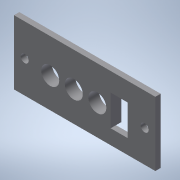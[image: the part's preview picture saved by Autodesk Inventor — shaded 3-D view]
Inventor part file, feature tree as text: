
AUTODESK INVENTOR PART (.ipt)
format: ipt  version: 2020 (Build 240168000, 168)  size: 364,544 bytes
history: native  units: in
note: dims shown in document units (in); Inventor stores cm internally (conversion verified against a paired STEP export)
features: extrude x2, sketch x2
ambient origin geometry x8: Origin, YZ Plane, XZ Plane, XY Plane, X Axis, Y Axis, Z Axis, Center Point
bodies: Body1 (feature_tree)
feature tree (4):
  extrude  "Extrusion6"  Depth=0.125in
  extrude  "Extrusion8"  Depth=0.0625in
  sketch  "Sketch1"  dims[d4=0.75in d5=0.125in]
  sketch  "Sketch7"  dims[d6=0.125in d34=0.0938in d38=0.375in d40=0.375in d41=1.6503in d59=0.21in d60=0.2in d61=0.36in d62=0.0238in d63=0.275in d64=0.275in d65=0.155in d66=0.15in d68=0.0625in d69=0.0in d70=0.12in d71=0.12in d72=0.025in d75=0.0in d76=0.0in d77=0.0625in d78=0.0in]
